FCSTD DOCUMENT  (FreeCAD 1.0R39285 (Git))
Label: mintyCube
License: All rights reserved
LicenseURL: https://en.wikipedia.org/wiki/All_rights_reserved
objects: Part::Cylinder×42, Part::Feature×41, Part::MultiFuse×27, Part::Box×18, Part::Cut×18, Part::Fillet×18, Sketcher::SketchObject×11, Part::Extrusion×10, App::Part×5, Part::FeaturePython×3, Part::Scale×3
note: 202 computed .brp shape members not serialized (recipe doc carries the construction recipe); baked Part::Feature solids carry a one-line shape summary decoded from their .brp

FEATURE [Part::Box] Box  label="outer"
  AttacherType = Attacher::AttachEngine3D
  Height = 79
  Length = 90
  Width = 90
FEATURE [Part::Box] Box001  label="inner"
  AttacherType = Attacher::AttachEngine3D
  Height = 74
  Length = 80
  Placement = pos=(5,5,0) rot=(0,0,1;0rad)
  Width = 80
FEATURE [Part::Cut] Cut  label="hollow_cut"
  Base = -> Box
  Refine = true
  Tool = -> Box001
FEATURE [Part::Fillet] Fillet  label="topCover"
  Base = -> Cut
  EdgeLinks = -> Cut [Edge1,Edge2,Edge3,Edge6,Edge7,Edge8,Edge9,Edge11,Edge17,Edge18,Edge19,Edge20,Edge21,Edge22,Edge23,Edge24]
  Edges = 16 edges: [Edge1 r=8,Edge2 r=8,Edge3 r=8,Edge6 r=8,Edge7 r=8,Edge8 r=8,Edge9 r=8,Edge11 r=8,Edge17 r=7,Edge18 r=7,Edge19 r=7,Edge20 r=7,Edge21 r=7,Edge22 r=7,Edge23 r=7,Edge24 r=7]
  Placement = pos=(0,0,6) rot=(0,0,1;0rad)
FEATURE [Part::Feature] Part__Feature010  label="ips7100"
  Placement = pos=(67.5,20.25,11.095) rot=(0,0,1;0rad)
  shape: bbox 48.08 x 13.99 x 44.08 mm, 1935 faces (baked)
FEATURE [Part::Cylinder] Cylinder003
  Angle = 360
  AttacherType = Attacher::AttachEngine3D
  FirstAngle = 0
  Height = 1
  Placement = pos=(0,0,-25) rot=(0,0,1;0rad)
  Radius = 23
  SecondAngle = 0
FEATURE [Part::Feature] Part__Feature3679  label="Sheel001"
  shape: bbox 121.8 x 121.8 x 8.7 mm, 646 faces (baked)
FEATURE [Part::MultiFuse] Fusion024  label="base001"
  Refine = true
  Shapes = -> [Part__Feature3679,Cylinder003]
FEATURE [Part::FeaturePython] Clone  label="base002"  # Draft clone (typed FeaturePython)
  AttacherType = Attacher::AttachEngine3D
  Fuse = false
  Objects = -> [Fusion024]
  Placement = pos=(45,45,11.66) rot=(0,0,1;0rad)
  Scale = (0.629921,0.629921,0.629921)
FEATURE [Sketcher::SketchObject] Sketch
  ArcFitTolerance = 1e-06
  FullyConstrained = true
  MakeInternals = false
  sketch-geometry (11):
    g0: LineSegment StartX=8 StartY=0 StartZ=0 EndX=82 EndY=0 EndZ=0
    g1: LineSegment StartX=90 StartY=8 StartZ=0 EndX=90 EndY=82 EndZ=0
    g2: LineSegment StartX=82 StartY=90 StartZ=0 EndX=8 EndY=90 EndZ=0
    g3: LineSegment StartX=0 StartY=82 StartZ=0 EndX=0 EndY=8 EndZ=0
    g4: ArcOfCircle CenterX=8 CenterY=8 CenterZ=0 NormalX=0 NormalY=0 NormalZ=1 AngleXU=0 Radius=8 StartAngle=3.14159 EndAngle=4.71239
    g5: ArcOfCircle CenterX=82 CenterY=8 CenterZ=0 NormalX=0 NormalY=0 NormalZ=1 AngleXU=0 Radius=8 StartAngle=4.71239 EndAngle=6.28319
    g6: ArcOfCircle CenterX=82 CenterY=82 CenterZ=0 NormalX=0 NormalY=0 NormalZ=1 AngleXU=0 Radius=8 StartAngle=-1.07e-14 EndAngle=1.5708
    g7: ArcOfCircle CenterX=8 CenterY=82 CenterZ=0 NormalX=0 NormalY=0 NormalZ=1 AngleXU=0 Radius=8 StartAngle=1.5708 EndAngle=3.14159
    g8: GeomPoint [constr] X=0 Y=0 Z=0
    g9: GeomPoint [constr] X=90 Y=90 Z=0
    g10: Circle CenterX=45 CenterY=45 CenterZ=0 NormalX=0 NormalY=0 NormalZ=1 AngleXU=0 Radius=36
  constraints (26):
    c: Tangent(g0,g4) = -1.5708
    c: Tangent(g0,g5) = -1.5708
    c: Tangent(g1,g5) = -1.5708
    c: Tangent(g1,g6) = -1.5708
    c: Tangent(g2,g6) = -1.5708
    c: Tangent(g2,g7) = -1.5708
    c: Tangent(g3,g7) = -1.5708
    c: Tangent(g3,g4) = -1.5708
    c: Horizontal(g0)
    c: Horizontal(g2)
    c: Vertical(g1)
    c: Vertical(g3)
    c: Equal(g4,g5)
    c: Equal(g5,g6)
    c: Equal(g6,g7)
    c: PointOnObject(g8,g0)
    c: PointOnObject(g8,g3)
    c: PointOnObject(g9,g1)
    c: PointOnObject(g9,g2)
    c: Radius(g5) = 8
    c: Coincident(g8,g-1)
    c: Distance(g-1,g2) = 90
    c: Distance(g-2,g1) = 90
    c: DistanceY(g-1,g10) = 45
    c: DistanceX(g-1,g10) = 45
    c: Diameter(g10) = 72
FEATURE [Part::Extrusion] Extrude  label="basePlate"
  Base = -> Sketch
  Dir = (0,0,1)
  DirMode = 2
  FaceMakerClass = Part::FaceMakerBullseye
  FaceMakerMode = 3
  LengthFwd = 11
  LengthRev = 0
  Solid = true
  Symmetric = false
FEATURE [Part::Fillet] Fillet001
  Base = -> Extrude
  EdgeLinks = -> Extrude [Edge26]
  Edges = 1 edges r=1: [Edge26]
FEATURE [Part::MultiFuse] Fusion  label="joinedBase"
  Placement = pos=(0,0,-5) rot=(0,0,1;0rad)
  Refine = true
  Shapes = -> [Clone,Fillet001]
FEATURE [Part::Fillet] Fillet002  label="Bottom"
  Base = -> Fusion
  EdgeLinks = -> Fusion [Edge1318,Edge1319,Edge1320,Edge1321,Edge1322,Edge1323,Edge1324,Edge1325]
  Edges = 8 edges r=7: [Edge1318,Edge1319,Edge1320,Edge1321,Edge1322,Edge1323,Edge1324,Edge1325]
FEATURE [Sketcher::SketchObject] Sketch001
  ArcFitTolerance = 1e-06
  FullyConstrained = true
  MakeInternals = false
  sketch-geometry (16):
    g0: LineSegment StartX=24 StartY=34 StartZ=0 EndX=24 EndY=24 EndZ=0
    g1: LineSegment StartX=24 StartY=24 StartZ=0 EndX=34 EndY=24 EndZ=0
    g2: LineSegment StartX=34 StartY=24 StartZ=0 EndX=34 EndY=34 EndZ=0
    g3: LineSegment StartX=34 StartY=34 StartZ=0 EndX=24 EndY=34 EndZ=0
    g4: LineSegment StartX=66 StartY=34 StartZ=0 EndX=66 EndY=24 EndZ=0
    g5: LineSegment StartX=66 StartY=24 StartZ=0 EndX=56 EndY=24 EndZ=0
    g6: LineSegment StartX=56 StartY=24 StartZ=0 EndX=56 EndY=34 EndZ=0
    g7: LineSegment StartX=56 StartY=34 StartZ=0 EndX=66 EndY=34 EndZ=0
    g8: LineSegment StartX=24 StartY=66 StartZ=0 EndX=24 EndY=56 EndZ=0
    g9: LineSegment StartX=24 StartY=56 StartZ=0 EndX=34 EndY=56 EndZ=0
    g10: LineSegment StartX=34 StartY=56 StartZ=0 EndX=34 EndY=66 EndZ=0
    g11: LineSegment StartX=34 StartY=66 StartZ=0 EndX=24 EndY=66 EndZ=0
    g12: LineSegment StartX=56 StartY=66 StartZ=0 EndX=56 EndY=56 EndZ=0
    g13: LineSegment StartX=56 StartY=56 StartZ=0 EndX=66 EndY=56 EndZ=0
    g14: LineSegment StartX=66 StartY=56 StartZ=0 EndX=66 EndY=66 EndZ=0
    g15: LineSegment StartX=66 StartY=66 StartZ=0 EndX=56 EndY=66 EndZ=0
  constraints (48):
    c: Coincident(g0,g1)
    c: Coincident(g1,g2)
    c: Coincident(g2,g3)
    c: Coincident(g3,g0)
    c: Vertical(g0)
    c: Vertical(g2)
    c: Horizontal(g1)
    c: Horizontal(g3)
    c: Coincident(g4,g5)
    c: Coincident(g5,g6)
    c: Coincident(g6,g7)
    c: Coincident(g7,g4)
    c: Vertical(g4)
    c: Vertical(g6)
    c: Horizontal(g5)
    c: Horizontal(g7)
    c: DistanceX(g1,g1) = 10
    c: Distance(g-1,g1) = 24
    c: DistanceX(g-1,g0) = 24
    c: DistanceY(g0,g0) = 10
    c: Distance(g4,g-1) = 24
    c: Distance(g4,g-2) = 66
    c: Distance(g5,g5) = 10
    c: DistanceY(g4,g4) = 10
    c: Coincident(g8,g9)
    c: Coincident(g9,g10)
    c: Coincident(g10,g11)
    c: Coincident(g11,g8)
    c: Vertical(g8)
    c: Vertical(g10)
    c: Horizontal(g9)
    c: Horizontal(g11)
    c: Coincident(g12,g13)
    c: Coincident(g13,g14)
    c: Coincident(g14,g15)
    c: Coincident(g15,g12)
    c: Vertical(g12)
    c: Vertical(g14)
    c: Horizontal(g13)
    c: Horizontal(g15)
    c: DistanceY(g8,g8) = 10
    c: DistanceX(g9,g9) = 10
    c: Distance(g8,g-2) = 24
    c: Distance(g8,g-1) = 56
    c: DistanceY(g14,g14) = 10
    c: DistanceX(g15,g15) = 10
    c: Distance(g-1,g13) = 56
    c: Distance(g14,g-2) = 66
FEATURE [Part::Feature] Part__Feature334  label="CAPC-0805-T0.95-BN v012"
  Placement = pos=(-5.48627,2.66154,1.6) rot=(0,0,-1;1.5708rad)
  shape: bbox 1.35 x 2.1 x 0.95 mm, 42 faces (baked)
FEATURE [Part::Feature] Part__Feature335  label="CAPC-0805-T0.95-BN v013"
  Placement = pos=(-3.43627,2.66154,1.6) rot=(0,0,-1;1.5708rad)
  shape: bbox 1.35 x 2.1 x 0.95 mm, 42 faces (baked)
FEATURE [Part::Feature] Part__Feature336  label="CAPC-0603-T0.9-BN v009"
  Placement = pos=(-1.69987,-3.28475,1.6) rot=(0,0,1;0rad)
  shape: bbox 1.7 x 0.9 x 0.9 mm, 42 faces (baked)
FEATURE [Part::Feature] Part__Feature337  label="BODY_MF06A003"
  Placement = pos=(0,0,0.762) rot=(0.57735,-0.57735,-0.57735;2.0944rad)
  shape: bbox 1.601 x 2.921 x 1.016 mm, 42 faces (baked)
FEATURE [Part::Feature] Part__Feature338  label="LEAD_MF06A018"
  Placement = pos=(-0.9652,-0.9525,0.1016) rot=(0.57735,-0.57735,-0.57735;2.0944rad)
  shape: bbox 0.6223 x 0.3749 x 0.8636 mm, 14 faces (baked)
FEATURE [Part::Feature] Part__Feature339  label="LEAD_MF06A019"
  Placement = pos=(-0.9652,0,0.1016) rot=(0.57735,-0.57735,-0.57735;2.0944rad)
  shape: bbox 0.6223 x 0.3749 x 0.8636 mm, 14 faces (baked)
FEATURE [Part::Feature] Part__Feature340  label="LEAD_MF06A020"
  Placement = pos=(-0.9652,0.9525,0.1016) rot=(0.57735,-0.57735,-0.57735;2.0944rad)
  shape: bbox 0.6223 x 0.3749 x 0.8636 mm, 14 faces (baked)
FEATURE [Part::Feature] Part__Feature341  label="LEAD_MF06A021"
  Placement = pos=(0.9652,-0.9525,0.1016) rot=(0.57735,0.57735,0.57735;2.0944rad)
  shape: bbox 0.6223 x 0.3749 x 0.8636 mm, 14 faces (baked)
FEATURE [Part::Feature] Part__Feature342  label="LEAD_MF06A022"
  Placement = pos=(0.9652,0,0.1016) rot=(0.57735,0.57735,0.57735;2.0944rad)
  shape: bbox 0.6223 x 0.3749 x 0.8636 mm, 14 faces (baked)
FEATURE [Part::Feature] Part__Feature343  label="LEAD_MF06A023"
  Placement = pos=(0.9652,0.9525,0.1016) rot=(0.57735,0.57735,0.57735;2.0944rad)
  shape: bbox 0.6223 x 0.3749 x 0.8636 mm, 14 faces (baked)
FEATURE [Part::Feature] Part__Feature344  label="SOT363 v005"
  Placement = pos=(4.97054,-0.645171,1.675) rot=(0,0,1;3.14159rad)
  shape: bbox 2.1 x 2 x 1.1 mm, 94 faces, 7 solids (baked)
FEATURE [Part::Feature] Part__Feature345  label="LED 0603 single color v005"
  Placement = pos=(-9.18406,3.72778,1.60762) rot=(0,0,1;1.5708rad)
  shape: bbox 1.961 x 0.7932 x 0.7145 mm, 63 faces, 5 solids (baked)
FEATURE [Part::Feature] Part__Feature346  label="RESC-0603 v007"
  Placement = pos=(4.83432,-3.67461,1.6) rot=(0,0,1;0rad)
  shape: bbox 1.7 x 0.9 x 0.55 mm, 52 faces, 3 solids (baked)
FEATURE [Part::Feature] Part__Feature347  label="RESC-0603 v008"
  Placement = pos=(-7.14949,3.61248,1.6) rot=(0,0,-1;1.5708rad)
  shape: bbox 0.9 x 1.7 x 0.55 mm, 52 faces, 3 solids (baked)
FEATURE [Part::Feature] Part__Feature348  label="Printed Circuit Board004"
  shape: bbox 25.4 x 17.78 x 1.6 mm, 42 faces (baked)
FEATURE [Part::Feature] Part__Feature349  label="EAHC2835WD009"
  shape: bbox 3.513 x 2.813 x 0.7485 mm, 108 faces, 4 solids (baked)
FEATURE [Part::Feature] Part__Feature350  label="AS7341 v005"
  Placement = pos=(0,-0.339822,1.6) rot=(0,0,1;0rad)
  shape: bbox 2 x 3.1 x 1.1 mm, 267 faces, 26 solids (baked)
FEATURE [Part::Feature] Part__Feature351  label="CAPC-0805-T0.95-BN v014"
  Placement = pos=(-5.01759,-3.15294,1.6) rot=(0,0,1;0rad)
  shape: bbox 2.1 x 1.35 x 0.95 mm, 42 faces (baked)
FEATURE [Part::Feature] Part__Feature352  label="YC164_RESPACK v007"
  Placement = pos=(2.99591,1.52916,1.6) rot=(0,0,1;0rad)
  shape: bbox 3.2 x 1.6 x 0.61 mm, 172 faces (baked)
FEATURE [Part::Feature] Part__Feature353  label="qwicc v009"
  Placement = pos=(-10.8364,0.0607456,1.65) rot=(0,0,-1;1.5708rad)
  shape: bbox 4.95 x 6 x 2.96 mm, 229 faces, 7 solids (baked)
FEATURE [Part::Feature] Part__Feature354  label="qwicc v010"
  Placement = pos=(10.8256,0.00556102,1.65) rot=(0,0,1;1.5708rad)
  shape: bbox 4.95 x 6 x 2.96 mm, 229 faces, 7 solids (baked)
FEATURE [App::Part] sot_23_6_v005  label="sot-23-6 v005"
  Group = -> [Part__Feature337,Part__Feature338,Part__Feature339,Part__Feature340,Part__Feature341,Part__Feature342,Part__Feature343]
  Origin = -> Origin091
  Placement = pos=(-4.47945,-0.603742,1.69152) rot=(0,0,1;0rad)
FEATURE [App::Part] Adafruit_AS7341_STEMMA_QT_v005  label="bme280"
  Group = -> [Part__Feature348,Part__Feature349,Part__Feature350,Part__Feature351,Part__Feature334,Part__Feature335,Part__Feature336,sot_23_6_v005,Part__Feature344,Part__Feature345,Part__Feature346,Part__Feature347,Part__Feature352,Part__Feature353,Part__Feature354]
  Origin = -> Origin092
  Placement = pos=(73,47.4039,34) rot=(-0.576812,0.578425,0.576812;4.1904rad)
FEATURE [Part::Box] Box002  label="Cube"
  AttacherType = Attacher::AttachEngine3D
  Height = 6
  Length = 19.2
  Width = 16.5
FEATURE [Part::Cylinder] Cylinder
  Angle = 360
  AttacherType = Attacher::AttachEngine3D
  FirstAngle = 0
  Height = 6
  Placement = pos=(9.6,21.3,0) rot=(0,0,1;0rad)
  Radius = 9.75
  SecondAngle = 0
FEATURE [Part::Box] Box003  label="Cube001"
  AttacherType = Attacher::AttachEngine3D
  Height = 6
  Length = 4.5
  Placement = pos=(13.42,28.5,0) rot=(0,0,1;5.49779rad)
  Width = 5
FEATURE [Part::Fillet] Fillet004
  Base = -> Box003
  EdgeLinks = -> Box003 [Edge3,Edge7]
  Edges = 2 edges r=2.24: [Edge3,Edge7]
FEATURE [Part::Fillet] Fillet005
  Base = -> Box002
  EdgeLinks = -> Box002 [Edge1,Edge3,Edge5,Edge7]
  Edges = 4 edges r=2: [Edge1,Edge3,Edge5,Edge7]
FEATURE [Part::Box] Box005  label="pcb"
  AttacherType = Attacher::AttachEngine3D
  Height = 0.8
  Length = 19.6
  Placement = pos=(-0.2,0,-0.8) rot=(0,0,1;0rad)
  Width = 31.1
FEATURE [Part::Box] Box006  label="Cube004"
  AttacherType = Attacher::AttachEngine3D
  Height = 6
  Length = 4.5
  Placement = pos=(2.6,25.3,0) rot=(0,0,-1;5.49779rad)
  Width = 5
FEATURE [Part::Fillet] Fillet006
  Base = -> Box006
  EdgeLinks = -> Box006 [Edge3,Edge7]
  Edges = 2 edges r=2.24: [Edge3,Edge7]
FEATURE [Part::MultiFuse] Fusion025
  Refine = true
  Shapes = -> [Cylinder,Fillet004,Fillet005,Fillet006]
FEATURE [Part::Fillet] Fillet007  label="COZIR-LP-5000"
  Base = -> Fusion025
  EdgeLinks = -> Fusion025 [Edge2,Edge4,Edge20,Edge26,Edge28,Edge44]
  Edges = 6 edges: [Edge2 r=2,Edge4 r=2,Edge20 r=2,Edge26 r=1,Edge28 r=2,Edge44 r=1]
FEATURE [Part::Feature] Part__Feature3681  label="Document"
  shape: bbox 7.62 x 3.4 x 1.5 mm, 124 faces (baked)
FEATURE [Part::Feature] Part__Feature3682  label="Document001"
  shape: bbox 0.4 x 0.4 x 7.6 mm, 14 faces (baked)
FEATURE [Part::Feature] Part__Feature3683  label="Document002"
  shape: bbox 0.4 x 0.4 x 7.6 mm, 14 faces (baked)
FEATURE [Part::Feature] Part__Feature3684  label="Document003"
  shape: bbox 0.4 x 0.4 x 7.6 mm, 14 faces (baked)
FEATURE [Part::Feature] Part__Feature3685  label="Document004"
  shape: bbox 0.4 x 0.4 x 7.6 mm, 14 faces (baked)
FEATURE [Part::Feature] Part__Feature3686  label="Document005"
  shape: bbox 0.4 x 0.4 x 7.6 mm, 14 faces (baked)
FEATURE [Part::Feature] Part__Feature3687  label="Document006"
  shape: bbox 0.4 x 0.4 x 7.6 mm, 14 faces (baked)
FEATURE [Part::Feature] Part__Feature3688  label="Document007"
  shape: bbox 0.4 x 0.4 x 7.6 mm, 14 faces (baked)
FEATURE [Part::Feature] Part__Feature3689  label="Document008"
  shape: bbox 0.4 x 0.4 x 7.6 mm, 14 faces (baked)
FEATURE [Part::Feature] Part__Feature3690  label="Document009"
  shape: bbox 0.4 x 0.4 x 7.6 mm, 14 faces (baked)
FEATURE [Part::Feature] Part__Feature3691  label="Document010"
  shape: bbox 0.4 x 0.4 x 7.6 mm, 14 faces (baked)
FEATURE [Part::Feature] Part__Feature3692  label="Document011"
  shape: bbox 0.4 x 0.4 x 7.6 mm, 14 faces (baked)
FEATURE [Part::Feature] Part__Feature3693  label="Document012"
  shape: bbox 0.4 x 0.4 x 7.6 mm, 14 faces (baked)
FEATURE [App::Part] Document  label="Document013"
  Group = -> [Part__Feature3681,Part__Feature3682,Part__Feature3683,Part__Feature3684,Part__Feature3685,Part__Feature3686,Part__Feature3687,Part__Feature3688,Part__Feature3689,Part__Feature3690,Part__Feature3691,Part__Feature3692,Part__Feature3693]
  Origin = -> Origin093
  Placement = pos=(9.8,26.75,-0.7) rot=(0,-1,0;3.14159rad)
FEATURE [Part::Cylinder] Cylinder004
  Angle = 360
  AttacherType = Attacher::AttachEngine3D
  FirstAngle = 0
  Height = 1
  Placement = pos=(0,0,-25) rot=(0,0,1;0rad)
  Radius = 23
  SecondAngle = 0
FEATURE [Part::Feature] Part__Feature3694  label="Sheel002"
  shape: bbox 121.8 x 121.8 x 8.7 mm, 646 faces (baked)
FEATURE [Part::MultiFuse] Fusion026  label="base004"
  Refine = true
  Shapes = -> [Part__Feature3694,Cylinder004]
FEATURE [Part::FeaturePython] Clone001  label="base003"  # Draft clone (typed FeaturePython)
  AttacherType = Attacher::AttachEngine3D
  Fuse = false
  Objects = -> [Fusion026]
  Placement = pos=(45,45,6.66) rot=(0,0,1;0rad)
  Scale = (0.629921,0.629921,0.629921)
FEATURE [Part::Scale] Scale
  Base = -> Clone001
  Placement = pos=(45.45,45.45,6.99) rot=(0,0,1;0rad)
  Uniform = true
  UniformScale = 0.99
  XScale = 1
  YScale = 1
  ZScale = 1
FEATURE [Part::Cylinder] Cylinder005
  Angle = 360
  AttacherType = Attacher::AttachEngine3D
  FirstAngle = 0
  Height = 1
  Placement = pos=(0,0,-25) rot=(0,0,1;0rad)
  Radius = 23
  SecondAngle = 0
FEATURE [Part::Feature] Part__Feature3695  label="Sheel003"
  shape: bbox 121.8 x 121.8 x 8.7 mm, 646 faces (baked)
FEATURE [Part::MultiFuse] Fusion027  label="base006"
  Refine = true
  Shapes = -> [Part__Feature3695,Cylinder005]
FEATURE [Part::FeaturePython] Clone002  label="base005"  # Draft clone (typed FeaturePython)
  AttacherType = Attacher::AttachEngine3D
  Fuse = false
  Objects = -> [Fusion027]
  Placement = pos=(45,45,11.66) rot=(0,0,1;0rad)
  Scale = (0.629921,0.629921,0.629921)
FEATURE [Part::Scale] Scale001
  Base = -> Clone002
  Placement = pos=(45.9,45.9,7.5) rot=(0,0,1;0rad)
  Uniform = true
  UniformScale = 0.98
  XScale = 1
  YScale = 1
  ZScale = 1
FEATURE [Sketcher::SketchObject] Sketch002
  ArcFitTolerance = 1e-06
  FullyConstrained = true
  MakeInternals = false
  sketch-geometry (4):
    g0: ArcOfCircle CenterX=0 CenterY=1.25 CenterZ=0 NormalX=0 NormalY=0 NormalZ=1 AngleXU=0 Radius=2 StartAngle=1e-16 EndAngle=3.14159
    g1: ArcOfCircle CenterX=0 CenterY=-1.25 CenterZ=0 NormalX=0 NormalY=0 NormalZ=1 AngleXU=0 Radius=2 StartAngle=3.14159 EndAngle=6.28319
    g2: LineSegment StartX=2 StartY=1.25 StartZ=0 EndX=2 EndY=-1.25 EndZ=0
    g3: LineSegment StartX=-2 StartY=1.25 StartZ=0 EndX=-2 EndY=-1.25 EndZ=0
  constraints (9):
    c: Tangent(g0,g2) = 1.5708
    c: Tangent(g0,g3) = -1.5708
    c: Tangent(g1,g2) = 1.5708
    c: Tangent(g1,g3) = -1.5708
    c: Equal(g0,g1)
    c: Distance(g0,g1) = 2.5
    c: Symmetric(g0,g1,g-1)
    c: Distance(g-2,g3) = 2
    c: Distance(g-1,g2) = 2
FEATURE [Part::Extrusion] Extrude001
  Base = -> Sketch002
  Dir = (0,0,1)
  DirMode = 2
  FaceMakerClass = Part::FaceMakerBullseye
  FaceMakerMode = 3
  LengthFwd = 2.5
  LengthRev = 0
  Placement = pos=(21.9086,21.9086,-7.10396) rot=(-0.627483,0.259912,-0.733969;1.02758rad)
  Solid = true
  Symmetric = false
FEATURE [Part::Extrusion] Extrude002
  Base = -> Sketch001
  Dir = (0,0,1)
  DirMode = 2
  FaceMakerClass = Part::FaceMakerBullseye
  FaceMakerMode = 3
  LengthFwd = 7
  LengthRev = 0
  Placement = pos=(0,0,-7.2) rot=(0,0,1;0rad)
  Solid = true
  Symmetric = false
FEATURE [Part::Fillet] Fillet008
  Base = -> Extrude002
  EdgeLinks = -> Extrude002 [Edge13,Edge14,Edge17,Edge20,Edge25,Edge26,Edge29,Edge32,Edge37,Edge38,Edge41,Edge44,Edge1,Edge2,Edge5,Edge8]
  Edges = 16 edges r=2: [Edge13,Edge14,Edge17,Edge20,Edge25,Edge26,Edge29,Edge32,Edge37,Edge38,Edge41,Edge44,Edge1,Edge2,Edge5,Edge8]
FEATURE [Part::MultiFuse] Fusion028  label="base_w_FanMount"
  Refine = true
  Shapes = -> [Scale001,Fillet008]
FEATURE [Part::Feature] Part__Feature3696  label="MF40100V1-1000U-A99"
  Placement = pos=(45,45,11) rot=(0,0,1;1.5708rad)
  shape: bbox 40.67 x 41.26 x 10.95 mm, 507 faces (baked)
FEATURE [Part::Cylinder] Cylinder007
  Angle = 180
  AttacherType = Attacher::AttachEngine3D
  FirstAngle = 0
  Height = 66
  Placement = pos=(12,5,66) rot=(-0.57735,-0.57735,-0.57735;4.18879rad)
  Radius = 3
  SecondAngle = 0
FEATURE [Part::Cylinder] Cylinder006
  Angle = 240
  AttacherType = Attacher::AttachEngine3D
  FirstAngle = 0
  Height = 66
  Placement = pos=(12,1.84e-14,66) rot=(0.694747,-0.186157,0.694747;3.50969rad)
  Radius = 5
  SecondAngle = 0
FEATURE [Part::Cylinder] Cylinder008
  Angle = 210
  AttacherType = Attacher::AttachEngine3D
  FirstAngle = 0
  Height = 66
  Placement = pos=(12,1.43e-14,61) rot=(0.694747,0.186157,0.694747;2.77349rad)
  Radius = 5
  SecondAngle = 0
FEATURE [Part::MultiFuse] Fusion029
  Refine = true
  Shapes = -> [Cylinder006,Cylinder007,Cylinder008]
FEATURE [Part::Fillet] Fillet010  label="ventcutLeft"
  Base = -> Fusion029
  EdgeLinks = -> Fusion029 [Edge1,Edge3,Edge11,Edge16]
  Edges = 4 edges: [Edge1 r=1,Edge3 r=1,Edge11 r=1,Edge16 r=0.5]
  Placement = pos=(2e-14,90,0) rot=(0,0,1;4.71239rad)
FEATURE [Part::Cylinder] Cylinder009
  Angle = 240
  AttacherType = Attacher::AttachEngine3D
  FirstAngle = 0
  Height = 66
  Placement = pos=(12,1.84e-14,66) rot=(0.694747,-0.186157,0.694747;3.50969rad)
  Radius = 5
  SecondAngle = 0
FEATURE [Part::Cylinder] Cylinder010
  Angle = 180
  AttacherType = Attacher::AttachEngine3D
  FirstAngle = 0
  Height = 66
  Placement = pos=(12,5,66) rot=(-0.57735,-0.57735,-0.57735;4.18879rad)
  Radius = 3
  SecondAngle = 0
FEATURE [Part::Cylinder] Cylinder011
  Angle = 210
  AttacherType = Attacher::AttachEngine3D
  FirstAngle = 0
  Height = 66
  Placement = pos=(12,1.43e-14,61) rot=(0.694747,0.186157,0.694747;2.77349rad)
  Radius = 5
  SecondAngle = 0
FEATURE [Part::MultiFuse] Fusion030
  Refine = true
  Shapes = -> [Cylinder009,Cylinder010,Cylinder011]
FEATURE [Part::Fillet] Fillet011  label="ventcutRight"
  Base = -> Fusion030
  EdgeLinks = -> Fusion030 [Edge1,Edge3,Edge11,Edge16]
  Edges = 4 edges: [Edge1 r=1,Edge3 r=1,Edge11 r=1,Edge16 r=0.5]
  Placement = pos=(90,-2e-14,0) rot=(0,0,1;1.5708rad)
FEATURE [Part::MultiFuse] Fusion031  label="ventcut"
  Refine = true
  Shapes = -> [Fillet010,Fillet011]
FEATURE [Part::Cut] Cut001  label="topCoverVented"
  Base = -> Fillet
  Refine = true
  Tool = -> Fusion031
FEATURE [Part::Box] Box007  label="Inner"
  AttacherType = Attacher::AttachEngine3D
  Height = 16
  Length = 20
  Placement = pos=(-0.4,-0.5,-2.5) rot=(0,0,1;0rad)
  Width = 44
FEATURE [Part::Box] Box008  label="Outer"
  AttacherType = Attacher::AttachEngine3D
  Height = 15
  Length = 28
  Placement = pos=(-4.4,-3.5,-6) rot=(0,0,1;0rad)
  Width = 35
FEATURE [Part::Cut] Cut002  label="slotCut"
  Base = -> Box008
  Refine = true
  Tool = -> Box007
FEATURE [Part::Box] Box009  label="Cube007"
  AttacherType = Attacher::AttachEngine3D
  Height = 2.75
  Length = 20
  Placement = pos=(-0.4,-0.5,6.25) rot=(0,0,1;0rad)
  Width = 32
FEATURE [Part::Cylinder] Cylinder012
  Angle = 360
  AttacherType = Attacher::AttachEngine3D
  FirstAngle = 0
  Height = 2
  Placement = pos=(9.6,21.3,4.1) rot=(0,0,1;0rad)
  Radius = 9
  SecondAngle = 0
FEATURE [App::Part] Part  label="Cozir"
  Group = -> [Document,Box002,Cylinder,Box003,Fillet004,Fillet005,Box006,Fillet006,Fusion025,Fillet007,Box005,Cylinder012]
  Origin = -> Origin094
  Placement = pos=(5.5,47,35) rot=(0,0,1;4.71239rad)
FEATURE [Part::Box] Box010  label="Cube008"
  AttacherType = Attacher::AttachEngine3D
  Height = 10
  Length = 10
  Placement = pos=(4.8,24,-6) rot=(0,0,1;0rad)
  Width = 20
FEATURE [Part::Cylinder] Cylinder013
  Angle = 360
  AttacherType = Attacher::AttachEngine3D
  FirstAngle = 0
  Height = 5
  Placement = pos=(9.6,21.3,4.1) rot=(0,0,1;0rad)
  Radius = 10
  SecondAngle = 0
FEATURE [Part::MultiFuse] Fusion032  label="sltCover"
  Refine = true
  Shapes = -> [Cut002,Box009]
FEATURE [Part::Cut] Cut003
  Base = -> Fusion032
  Refine = true
  Tool = -> Cylinder013
FEATURE [Part::Cut] Cut004  label="CozirHold"
  Base = -> Cut003
  Placement = pos=(5.5,47,35) rot=(0,0,1;4.71239rad)
  Refine = true
  Tool = -> Box010
FEATURE [Part::MultiFuse] Fusion033  label="topCover_CozirHold"
  Refine = true
  Shapes = -> [Cut001,Cut004]
FEATURE [Part::Box] Box027  label="bottom046"
  AttacherType = Attacher::AttachEngine3D
  Height = 39
  Length = 70
  Placement = pos=(2,2,2) rot=(0,0,1;0rad)
  Width = 87
FEATURE [Part::Box] Box031  label="bottom049"
  AttacherType = Attacher::AttachEngine3D
  Height = 27
  Length = 74
  Width = 91
FEATURE [Part::Fillet] Fillet046  label="bottom047"
  Base = -> Box031
  EdgeLinks = -> Box031 [Edge1,Edge3,Edge4,Edge5,Edge7,Edge8,Edge9,Edge11]
  Edges = 8 edges r=2: [Edge1,Edge3,Edge4,Edge5,Edge7,Edge8,Edge9,Edge11]
FEATURE [Part::Fillet] Fillet050  label="bottomCut013"
  Base = -> Box027
  EdgeLinks = -> Box027 [Edge1,Edge3,Edge4,Edge5,Edge7,Edge8,Edge9,Edge11]
  Edges = 8 edges r=2: [Edge1,Edge3,Edge4,Edge5,Edge7,Edge8,Edge9,Edge11]
FEATURE [Part::Cut] Cut032  label="bottom052"
  Base = -> Fillet046
  Tool = -> Fillet050
FEATURE [Sketcher::SketchObject] Sketch171
  ArcFitTolerance = 0
  AttachmentSupport = -> [Cut032]
  FullyConstrained = true
  MakeInternals = false
  MapMode = 2
  sketch-geometry (10):
    g0: LineSegment StartX=63 StartY=9.25 StartZ=0 EndX=78 EndY=9.25 EndZ=0
    g1: LineSegment StartX=78 StartY=9.25 StartZ=0 EndX=78 EndY=2 EndZ=0
    g2: LineSegment StartX=78 StartY=2 StartZ=0 EndX=63 EndY=2 EndZ=0
    g3: LineSegment StartX=63 StartY=2 StartZ=0 EndX=63 EndY=9.25 EndZ=0
    g4: LineSegment StartX=-5 StartY=9.25 StartZ=0 EndX=10 EndY=9.25 EndZ=0
    g5: LineSegment StartX=10 StartY=9.25 StartZ=0 EndX=10 EndY=2 EndZ=0
    g6: LineSegment StartX=10 StartY=2 StartZ=0 EndX=-5 EndY=2 EndZ=0
    g7: LineSegment StartX=-5 StartY=2 StartZ=0 EndX=-5 EndY=9.25 EndZ=0
    g8: Circle CenterX=7.47 CenterY=6.47 CenterZ=0 NormalX=0 NormalY=0 NormalZ=1 AngleXU=0 Radius=1.35
    g9: Circle CenterX=65.52 CenterY=6.47 CenterZ=0 NormalX=0 NormalY=0 NormalZ=1 AngleXU=0 Radius=1.35
  constraints (30):
    c: Coincident(g0,g1)
    c: Coincident(g1,g2)
    c: Coincident(g2,g3)
    c: Coincident(g3,g0)
    c: Horizontal(g0)
    c: Horizontal(g2)
    c: Vertical(g1)
    c: Vertical(g3)
    c: Coincident(g4,g5)
    c: Coincident(g5,g6)
    c: Coincident(g6,g7)
    c: Coincident(g7,g4)
    c: Horizontal(g4)
    c: Horizontal(g6)
    c: Vertical(g5)
    c: Vertical(g7)
    c: DistanceX(g6) = -5
    c: DistanceY(g6) = 2
    c: DistanceX(g6,g6) = 15
    c: DistanceY(g7,g7) = 7.25
    c: DistanceX(g-1,g1) = 78
    c: DistanceY(g2,g5) = 0
    c: DistanceY(g0,g4) = 0
    c: DistanceX(g2,g2) = 15
    c: DistanceX(g8) = 7.47
    c: Radius(g8) = 1.35
    c: DistanceX(g9) = 65.52
    c: DistanceY(g8,g9) = 0
    c: Radius(g9) = 1.35
    c: DistanceY(g8) = 6.47
FEATURE [Part::Extrusion] Extrude174  label="RaberryPiHold004"
  Base = -> Sketch171
  Dir = (0,0,1)
  DirMode = 2
  FaceMakerClass = Part::FaceMakerBullseye
  FaceMakerMode = 3
  LengthFwd = 2
  LengthRev = 0
  Placement = pos=(0,0,20.7) rot=(0,0,1;0rad)
  Solid = true
  Symmetric = false
FEATURE [Part::Fillet] Fillet044  label="piHoldBottomInDone004"
  Base = -> Extrude174
  EdgeLinks = -> Extrude174 [Edge16,Edge19,Edge27,Edge2,Edge4,Edge7]
  Edges = 6 edges: [Edge16 r=2,Edge19 r=1,Edge27 r=1,Edge2 r=2,Edge4 r=1,Edge7 r=1]
  Placement = pos=(8.5,87.5,73.5) rot=(-1,0,0;3.14159rad)
FEATURE [Part::Box] Box032  label="batteryPlus"
  AttacherType = Attacher::AttachEngine3D
  Height = 11
  Length = 68
  Placement = pos=(11,71,79) rot=(-1,0,0;3.14159rad)
  Width = 56
FEATURE [Sketcher::SketchObject] Sketch153
  ArcFitTolerance = 0
  FullyConstrained = true
  MakeInternals = false
  Placement = pos=(0,0,0) rot=(1,0,0;1.5708rad)
  sketch-geometry (40):
    g0: LineSegment StartX=40 StartY=24.5 StartZ=0 EndX=40 EndY=22 EndZ=0
    g1: LineSegment StartX=40 StartY=22 StartZ=0 EndX=42.5 EndY=19.5 EndZ=0
    g2: LineSegment StartX=42.5 StartY=19.5 StartZ=0 EndX=48.7 EndY=19.5 EndZ=0
    g3: LineSegment StartX=48.7 StartY=19.5 StartZ=0 EndX=51.2 EndY=22 EndZ=0
    g4: LineSegment StartX=51.2 StartY=22 StartZ=0 EndX=51.2 EndY=24.5 EndZ=0
    g5: LineSegment StartX=51.2 StartY=24.5 StartZ=0 EndX=40 EndY=24.5 EndZ=0
    g6: LineSegment StartX=52.45 StartY=24.5 StartZ=0 EndX=52.45 EndY=22 EndZ=0
    g7: LineSegment StartX=52.45 StartY=22 StartZ=0 EndX=54.95 EndY=19.5 EndZ=0
    g8: LineSegment StartX=54.95 StartY=19.5 StartZ=0 EndX=61.15 EndY=19.5 EndZ=0
    g9: LineSegment StartX=61.15 StartY=19.5 StartZ=0 EndX=63.65 EndY=22 EndZ=0
    g10: LineSegment StartX=63.65 StartY=22 StartZ=0 EndX=63.65 EndY=24.5 EndZ=0
    g11: LineSegment StartX=63.65 StartY=24.5 StartZ=0 EndX=52.45 EndY=24.5 EndZ=0
    g12: ArcOfCircle CenterX=12.3 CenterY=15.45 CenterZ=0 NormalX=0 NormalY=0 NormalZ=1 AngleXU=0 Radius=1 StartAngle=1.5708 EndAngle=3.14159
    g13: LineSegment StartX=11.3 StartY=15.45 StartZ=0 EndX=11.3 EndY=14.2 EndZ=0
    g14: LineSegment StartX=12.3 StartY=16.45 StartZ=0 EndX=16.8 EndY=16.45 EndZ=0
    g15: ArcOfCircle CenterX=16.8 CenterY=15.45 CenterZ=0 NormalX=0 NormalY=0 NormalZ=1 AngleXU=0 Radius=1 StartAngle=3e-16 EndAngle=1.5708
    g16: ArcOfCircle CenterX=16.8 CenterY=14.2 CenterZ=0 NormalX=0 NormalY=0 NormalZ=1 AngleXU=0 Radius=1 StartAngle=4.71239 EndAngle=6.28319
    g17: ArcOfCircle CenterX=12.3 CenterY=14.2 CenterZ=0 NormalX=0 NormalY=0 NormalZ=1 AngleXU=0 Radius=1 StartAngle=3.14159 EndAngle=4.71239
    g18: LineSegment StartX=12.3 StartY=13.2 StartZ=0 EndX=16.8 EndY=13.2 EndZ=0
    g19: LineSegment StartX=17.8 StartY=15.45 StartZ=0 EndX=17.8 EndY=14.2 EndZ=0
    g20: Circle CenterX=18.9 CenterY=16.475 CenterZ=0 NormalX=0 NormalY=0 NormalZ=1 AngleXU=0 Radius=0.5
    g21: Circle CenterX=21.09 CenterY=16.475 CenterZ=0 NormalX=0 NormalY=0 NormalZ=1 AngleXU=0 Radius=0.5
    g22: Circle CenterX=23.28 CenterY=16.475 CenterZ=0 NormalX=0 NormalY=0 NormalZ=1 AngleXU=0 Radius=0.5
    g23: Circle CenterX=25.47 CenterY=16.475 CenterZ=0 NormalX=0 NormalY=0 NormalZ=1 AngleXU=0 Radius=0.5
    g24: LineSegment StartX=44.8 StartY=16.45 StartZ=0 EndX=49.3 EndY=16.45 EndZ=0
    g25: LineSegment StartX=50.3 StartY=15.45 StartZ=0 EndX=50.3 EndY=14.2 EndZ=0
    g26: LineSegment StartX=49.3 StartY=13.2 StartZ=0 EndX=44.8 EndY=13.2 EndZ=0
    g27: LineSegment StartX=43.8 StartY=15.45 StartZ=0 EndX=43.8 EndY=14.2 EndZ=0
    g28: ArcOfCircle CenterX=44.8 CenterY=15.45 CenterZ=0 NormalX=0 NormalY=0 NormalZ=1 AngleXU=0 Radius=1 StartAngle=1.5708 EndAngle=3.14159
    g29: ArcOfCircle CenterX=49.3 CenterY=15.45 CenterZ=0 NormalX=0 NormalY=0 NormalZ=1 AngleXU=0 Radius=1 StartAngle=3e-16 EndAngle=1.5708
    g30: ArcOfCircle CenterX=49.3 CenterY=14.2 CenterZ=0 NormalX=0 NormalY=0 NormalZ=1 AngleXU=0 Radius=1 StartAngle=4.71239 EndAngle=6.28319
    g31: ArcOfCircle CenterX=44.8 CenterY=14.2 CenterZ=0 NormalX=0 NormalY=0 NormalZ=1 AngleXU=0 Radius=1 StartAngle=3.14159 EndAngle=4.71239
    g32: LineSegment StartX=52.25 StartY=15.58 StartZ=0 EndX=52.25 EndY=14.58 EndZ=0
    g33: LineSegment StartX=53.5 StartY=16.83 StartZ=0 EndX=60.5 EndY=16.83 EndZ=0
    g34: LineSegment StartX=53.5 StartY=13.33 StartZ=0 EndX=60.5 EndY=13.33 EndZ=0
    g35: LineSegment StartX=61.75 StartY=15.58 StartZ=0 EndX=61.75 EndY=14.58 EndZ=0
    g36: ArcOfCircle CenterX=53.5 CenterY=15.58 CenterZ=0 NormalX=0 NormalY=0 NormalZ=1 AngleXU=0 Radius=1.25 StartAngle=1.5708 EndAngle=3.14159
    g37: ArcOfCircle CenterX=60.5 CenterY=15.58 CenterZ=0 NormalX=0 NormalY=0 NormalZ=1 AngleXU=0 Radius=1.25 StartAngle=2e-16 EndAngle=1.5708
    g38: ArcOfCircle CenterX=60.5 CenterY=14.58 CenterZ=0 NormalX=0 NormalY=0 NormalZ=1 AngleXU=0 Radius=1.25 StartAngle=4.7124 EndAngle=6.28319
    g39: ArcOfCircle CenterX=53.5 CenterY=14.58 CenterZ=0 NormalX=0 NormalY=0 NormalZ=1 AngleXU=0 Radius=1.25 StartAngle=3.14159 EndAngle=4.71239
  constraints (132):
    c: Coincident(g0,g1)
    c: Coincident(g1,g2)
    c: Horizontal(g2)
    c: Coincident(g2,g3)
    c: Coincident(g3,g4)
    c: Vertical(g4)
    c: Coincident(g4,g5)
    c: Coincident(g5,g0)
    c: Coincident(g6,g7)
    c: Coincident(g7,g8)
    c: Horizontal(g8)
    c: Coincident(g8,g9)
    c: Coincident(g9,g10)
    c: Vertical(g10)
    c: Coincident(g10,g11)
    c: Coincident(g11,g6)
    c: Horizontal(g11)
    c: Horizontal(g5)
    c: Vertical(g0)
    c: Vertical(g6)
    c: DistanceX(g0) = 40
    c: DistanceX(g0,g4) = 11.2
    c: DistanceY(g6,g4) = 0
    c: DistanceY(g0,g0) = 2.5
    c: DistanceY(g3,g0) = 0
    c: DistanceY(g6,g3) = 0
    c: DistanceY(g9,g6) = 0
    c: DistanceY(g1,g0) = 2.5
    c: DistanceX(g0,g1) = 2.5
    c: DistanceX(g2,g3) = 2.5
    c: DistanceX(g4,g6) = 1.25
    c: DistanceY(g7,g2) = 0
    c: DistanceX(g6,g7) = 2.5
    c: DistanceX(g8,g9) = 2.5
    c: DistanceX(g6,g10) = 11.2
    c: DistanceY(g0) = 24.5
    c: Coincident(g13,g12)
    c: Vertical(g13)
    c: Horizontal(g14)
    c: Coincident(g15,g14)
    c: Coincident(g17,g13)
    c: Coincident(g18,g17)
    c: Coincident(g18,g16)
    c: Horizontal(g18)
    c: Coincident(g19,g15)
    c: Coincident(g19,g16)
    c: Vertical(g19)
    c: Coincident(g12,g14)
    c: Radius(g12) = 1
    c: Angle(g12) = 1.5708
    c: Angle(g15) = 1.5708
    c: Angle(g16) = 1.5708
    c: Angle(g17) = 1.5708
    c: DistanceX(g17) = 12.3
    c: DistanceY(g17) = 13.2
    c: DistanceX(g13) = 11.3
    c: DistanceY(g17,g13) = 0
    c: DistanceY(g12,g12) = 0
    c: DistanceX(g15,g14) = 0
    c: Radius(g15) = 1
    c: Radius(g16) = 1
    c: DistanceX(g16,g16) = 0
    c: DistanceX(g12,g14) = 4.5
    c: DistanceX(g20) = 18.9
    c: Radius(g20) = 0.5
    c: DistanceY(g20) = 16.475
    c: DistanceX(g20,g21) = 2.19
    c: DistanceY(g20,g21) = 0
    c: DistanceY(g22,g21) = 0
    c: DistanceY(g23,g22) = 0
    c: DistanceX(g21,g22) = 2.19
    c: Radius(g21) = 0.5
    c: Radius(g22) = 0.5
    c: Radius(g23) = 0.5
    c: DistanceX(g22,g23) = 2.19
    c: DistanceY(g17,g12) = 1.25
    c: Horizontal(g24)
    c: Vertical(g25)
    c: Vertical(g27)
    c: Coincident(g27,g28)
    c: Coincident(g27,g31)
    c: Coincident(g26,g31)
    c: Coincident(g26,g30)
    c: Coincident(g25,g30)
    c: Coincident(g25,g29)
    c: Coincident(g24,g29)
    c: Coincident(g24,g28)
    c: Angle(g28) = 1.5708
    c: Angle(g29) = 1.5708
    c: Angle(g31) = 1.5708
    c: Angle(g30) = 1.5708
    c: DistanceY(g12,g28) = 0
    c: DistanceY(g28,g27) = 0
    c: Radius(g28) = 1
    c: DistanceY(g27,g31) = 0
    c: Radius(g31) = 1
    c: Radius(g30) = 1
    c: Radius(g29) = 1
    c: DistanceY(g27,g17) = 0
    c: DistanceY(g25,g30) = 0
    c: Horizontal(g26)
    c: DistanceX(g29,g24) = 0
    c: DistanceX(g26,g26) = 4.5
    c: Vertical(g32)
    c: Horizontal(g33)
    c: Horizontal(g34)
    c: Vertical(g35)
    c: Coincident(g36,g32)
    c: Coincident(g36,g33)
    c: Coincident(g37,g33)
    c: Coincident(g39,g32)
    c: Coincident(g39,g34)
    c: Coincident(g34,g38)
    c: Coincident(g35,g38)
    c: Coincident(g35,g37)
    c: DistanceX(g36) = 53.5
    c: DistanceY(g36) = 15.58
    c: DistanceX(g36,g39) = 0
    c: DistanceY(g39,g36) = 1
    c: Radius(g36) = 1.25
    c: Radius(g38) = 1.25
    c: Radius(g37) = 1.25
    c: DistanceX(g39,g34) = 0
    c: DistanceX(g36,g33) = 0
    c: DistanceY(g36,g37) = 0
    c: DistanceY(g38,g39) = 0
    c: DistanceY(g39,g32) = 0
    c: DistanceX(g36,g37) = 7
    c: DistanceX(g12,g28) = 32.5
    c: DistanceY(g35,g38) = 0
    c: DistanceY(g37,g35) = 0
    c: Angle(g36) = 1.5708
FEATURE [Part::Extrusion] Extrude153  label="lightBottomCutDone004"
  Base = -> Sketch153
  Dir = (0,-1,2e-16)
  DirMode = 2
  FaceMakerClass = Part::FaceMakerBullseye
  FaceMakerMode = 3
  LengthFwd = 10
  LengthRev = 0
  Placement = pos=(8.25,84,74) rot=(-1,0,0;3.14159rad)
  Solid = true
  Symmetric = false
FEATURE [Part::Cut] Cut033  label="topCover_portCut"
  Base = -> Fusion033
  Refine = true
  Tool = -> Extrude153
FEATURE [Sketcher::SketchObject] Sketch172
  ArcFitTolerance = 1e-06
  FullyConstrained = true
  MakeInternals = false
  Placement = pos=(0,0,0) rot=(0,0.707107,0.707107;3.14159rad)
  sketch-geometry (4):
    g0: ArcOfCircle CenterX=-67 CenterY=55 CenterZ=0 NormalX=0 NormalY=0 NormalZ=1 AngleXU=0 Radius=10 StartAngle=1.5708 EndAngle=4.71239
    g1: ArcOfCircle CenterX=-23 CenterY=55 CenterZ=0 NormalX=0 NormalY=0 NormalZ=1 AngleXU=0 Radius=10 StartAngle=4.71239 EndAngle=7.85398
    g2: LineSegment StartX=-67 StartY=65 StartZ=0 EndX=-23 EndY=65 EndZ=0
    g3: LineSegment StartX=-67 StartY=45 StartZ=0 EndX=-23 EndY=45 EndZ=0
  constraints (10):
    c: Tangent(g0,g2) = 1.5708
    c: Tangent(g0,g3) = -1.5708
    c: Tangent(g1,g2) = 1.5708
    c: Tangent(g1,g3) = -1.5708
    c: Equal(g0,g1)
    c: Horizontal(g2)
    c: DistanceY(g1,g1) = 20
    c: Distance(g0,g-1) = 45
    c: Distance(g1,g-2) = 23
    c: DistanceX(g3,g3) = 44
FEATURE [Part::Extrusion] Extrude175
  Base = -> Sketch172
  Dir = (0,1,-2e-16)
  DirMode = 2
  FaceMakerClass = Part::FaceMakerBullseye
  FaceMakerMode = 3
  LengthFwd = 4
  LengthRev = 0
  Placement = pos=(0,86,0) rot=(0,0,1;0rad)
  Solid = true
  Symmetric = false
FEATURE [Part::Cut] Cut034
  Base = -> Cut033
  Refine = true
  Tool = -> Extrude175
FEATURE [Part::Fillet] Fillet051  label="topCoverFillet"
  Base = -> Cut034
  EdgeLinks = -> Cut034 [Edge67,Edge68,Edge69,Edge70,Edge91,Edge92,Edge93,Edge94,Edge151,Edge153,Edge155,Edge156,Edge183,Edge184,Edge185,Edge187,Edge188,Edge189,Edge190,Edge191,Edge192,Edge193,Edge194,Edge195,Edge288,Edge289,Edge290,Edge292,Edge293,Edge294,Edge298,Edge300,Edge301,Edge303,Edge304,Edge305,Edge306,Edge311,Edge314]
  Edges = 39 edges: [Edge67 r=2,Edge68 r=2,Edge69 r=2,Edge70 r=2,Edge91 r=2,Edge92 r=2,Edge93 r=2,Edge94 r=2,Edge151 r=1.5,Edge153 r=1.5,Edge155 r=1.5,Edge156 r=1.5,Edge183 r=1,Edge184 r=2,Edge185 r=2,Edge187 r=1,Edge188 r=2,Edge189 r=1,Edge190 r=1,Edge191 r=1,Edge192 r=1,Edge193 r=1,Edge194 r=2,Edge195 r=1,Edge288 r=2,Edge289 r=1,Edge290 r=1,Edge292 r=1,Edge293 r=1,Edge294 r=2,Edge298 r=2,Edge300 r=2,Edge301 r=1,Edge303 r=1,Edge304 r=1,Edge305 r=1,Edge306 r=1,Edge311 r=1,Edge314 r=1]
FEATURE [Sketcher::SketchObject] Sketch173
  ArcFitTolerance = 1e-06
  FullyConstrained = true
  MakeInternals = false
  Placement = pos=(0,0,0) rot=(1,0,0;3.14159rad)
  sketch-geometry (4):
    g0: Circle CenterX=12 CenterY=-12 CenterZ=0 NormalX=0 NormalY=0 NormalZ=1 AngleXU=0 Radius=1.625
    g1: Circle CenterX=78 CenterY=-12 CenterZ=0 NormalX=0 NormalY=0 NormalZ=1 AngleXU=0 Radius=1.625
    g2: Circle CenterX=12 CenterY=-78 CenterZ=0 NormalX=0 NormalY=0 NormalZ=1 AngleXU=0 Radius=1.625
    g3: Circle CenterX=78 CenterY=-78 CenterZ=0 NormalX=0 NormalY=0 NormalZ=1 AngleXU=0 Radius=1.625
  constraints (12):
    c: Equal(g0,g1)
    c: Equal(g0,g2)
    c: Equal(g0,g3)
    c: Diameter(g0) = 3.25
    c: Distance(g0,g-1) = 12
    c: Distance(g0,g-2) = 12
    c: Distance(g1,g-2) = 78
    c: Distance(g1,g-1) = 12
    c: Distance(g2,g-2) = 12
    c: Distance(g2,g-1) = 78
    c: DistanceY(g3,g-1) = 78
    c: DistanceX(g-1,g3) = 78
FEATURE [Part::Extrusion] Extrude176
  Base = -> Sketch173
  Dir = (0,0,-1)
  DirMode = 2
  FaceMakerClass = Part::FaceMakerBullseye
  FaceMakerMode = 3
  LengthFwd = 20
  LengthRev = 0
  Solid = true
  Symmetric = true
FEATURE [Sketcher::SketchObject] Sketch167
  ArcFitTolerance = 0
  FullyConstrained = true
  MakeInternals = false
  sketch-geometry (5):
    g0: ArcOfCircle CenterX=6.5 CenterY=41 CenterZ=0 NormalX=0 NormalY=0 NormalZ=1 AngleXU=0 Radius=5 StartAngle=4.71239 EndAngle=7.85398
    g1: LineSegment StartX=6.5 StartY=46 StartZ=0 EndX=2 EndY=46 EndZ=0
    g2: LineSegment StartX=6.5 StartY=36 StartZ=0 EndX=2 EndY=36 EndZ=0
    g3: LineSegment StartX=2 StartY=46 StartZ=0 EndX=2 EndY=36 EndZ=0
    g4: Circle CenterX=6.5 CenterY=41 CenterZ=0 NormalX=0 NormalY=0 NormalZ=1 AngleXU=0 Radius=1.65
  constraints (15):
    c: Coincident(g1,g0)
    c: Coincident(g2,g0)
    c: Horizontal(g2)
    c: Coincident(g3,g1)
    c: Coincident(g3,g2)
    c: Vertical(g3)
    c: Horizontal(g1)
    c: DistanceX(g0,g0) = 0
    c: DistanceX(g2) = 2
    c: DistanceY(g2) = 36
    c: DistanceY(g2,g1) = 10
    c: Angle(g0) = 3.14159
    c: DistanceX(g0) = 6.5
    c: Coincident(g4,g0)
    c: Radius(g4) = 1.65
FEATURE [Part::Extrusion] Extrude163  label="batteryHold01"
  Base = -> Sketch167
  Dir = (0,0,1)
  DirMode = 2
  FaceMakerClass = Part::FaceMakerBullseye
  FaceMakerMode = 3
  LengthFwd = 5
  LengthRev = 0
  Placement = pos=(4,87,66) rot=(0,0,1;4.71239rad)
  Solid = true
  Symmetric = false
FEATURE [Sketcher::SketchObject] Sketch174
  ArcFitTolerance = 0
  FullyConstrained = true
  MakeInternals = false
  sketch-geometry (5):
    g0: ArcOfCircle CenterX=6.5 CenterY=41 CenterZ=0 NormalX=0 NormalY=0 NormalZ=1 AngleXU=0 Radius=5 StartAngle=4.71239 EndAngle=7.85398
    g1: LineSegment StartX=6.5 StartY=46 StartZ=0 EndX=2 EndY=46 EndZ=0
    g2: LineSegment StartX=6.5 StartY=36 StartZ=0 EndX=2 EndY=36 EndZ=0
    g3: LineSegment StartX=2 StartY=46 StartZ=0 EndX=2 EndY=36 EndZ=0
    g4: Circle CenterX=6.5 CenterY=41 CenterZ=0 NormalX=0 NormalY=0 NormalZ=1 AngleXU=0 Radius=1.65
  constraints (15):
    c: Coincident(g1,g0)
    c: Coincident(g2,g0)
    c: Horizontal(g2)
    c: Coincident(g3,g1)
    c: Coincident(g3,g2)
    c: Vertical(g3)
    c: Horizontal(g1)
    c: DistanceX(g0,g0) = 0
    c: DistanceX(g2) = 2
    c: DistanceY(g2) = 36
    c: DistanceY(g2,g1) = 10
    c: Angle(g0) = 3.14159
    c: DistanceX(g0) = 6.5
    c: Coincident(g4,g0)
    c: Radius(g4) = 1.65
FEATURE [Part::Extrusion] Extrude177  label="batteryHold02"
  Base = -> Sketch174
  Dir = (0,0,1)
  DirMode = 2
  FaceMakerClass = Part::FaceMakerBullseye
  FaceMakerMode = 3
  LengthFwd = 5
  LengthRev = 0
  Placement = pos=(86,3,66) rot=(0,0,-1;4.71239rad)
  Solid = true
  Symmetric = false
FEATURE [Sketcher::SketchObject] Sketch175
  ArcFitTolerance = 1e-06
  FullyConstrained = false
  MakeInternals = false
  Placement = pos=(0,0,0) rot=(1,0,0;3.14159rad)
  sketch-geometry (12):
    g0: LineSegment StartX=25 StartY=-15 StartZ=0 EndX=75 EndY=-15 EndZ=0
    g1: LineSegment StartX=75 StartY=-15 StartZ=0 EndX=75 EndY=-71 EndZ=0
    g2: LineSegment StartX=75 StartY=-71 StartZ=0 EndX=25 EndY=-71 EndZ=0
    g3: LineSegment StartX=25 StartY=-71 StartZ=0 EndX=25 EndY=-64 EndZ=0
    g4: LineSegment StartX=25 StartY=-64 StartZ=0 EndX=70 EndY=-64 EndZ=0
    g5: LineSegment StartX=70 StartY=-64 StartZ=0 EndX=41.096 EndY=-43 EndZ=0
    g6: LineSegment StartX=41.096 StartY=-43 StartZ=0 EndX=70 EndY=-22 EndZ=0
    g7: LineSegment StartX=25 StartY=-15 StartZ=0 EndX=25 EndY=-22 EndZ=0
    g8: LineSegment StartX=25 StartY=-22 StartZ=0 EndX=70 EndY=-22 EndZ=0
    g9: LineSegment StartX=70 StartY=-28.5199 StartZ=0 EndX=49.3543 EndY=-43.5199 EndZ=0
    g10: LineSegment StartX=49.3543 StartY=-43.5199 StartZ=0 EndX=70 EndY=-58.5199 EndZ=0
    g11: LineSegment StartX=70 StartY=-58.5199 StartZ=0 EndX=70 EndY=-28.5199 EndZ=0
  constraints (34):
    c: Horizontal(g0)
    c: Coincident(g1,g0)
    c: Vertical(g1)
    c: Coincident(g2,g1)
    c: Horizontal(g2)
    c: Coincident(g3,g2)
    c: Vertical(g3)
    c: Coincident(g4,g3)
    c: Horizontal(g4)
    c: Coincident(g5,g4)
    c: Coincident(g6,g5)
    c: Coincident(g7,g0)
    c: Vertical(g7)
    c: Coincident(g8,g7)
    c: Coincident(g8,g6)
    c: Horizontal(g8)
    c: Coincident(g10,g9)
    c: Coincident(g11,g10)
    c: Coincident(g11,g9)
    c: Distance(g0,g-1) = 15
    c: Vertical(g11)
    c: DistanceX(g0,g0) = 50
    c: Distance(g1,g11) = 5
    c: DistanceY(g7,g7) = 7
    c: Equal(g6,g5)
    c: Distance(g0,g-2) = 25
    c: DistanceX(g8,g8) = 45
    c: DistanceX(g4,g4) = 45
    c: Distance(g3,g-2) = 25
    c: DistanceY(g3,g3) = 7
    c: DistanceY(g3,g7) = 42
    c: Equal(g9,g10)
    c: Angle(g8,g6) = 0.628319
    c: Angle(g8,g9) = 0.628319
FEATURE [Part::Cylinder] Cylinder014
  Angle = 240
  AttacherType = Attacher::AttachEngine3D
  FirstAngle = 0
  Height = 44
  Placement = pos=(12,1.84e-14,66) rot=(0.694747,-0.186157,0.694747;3.50969rad)
  Radius = 5
  SecondAngle = 0
FEATURE [Part::Cylinder] Cylinder015
  Angle = 180
  AttacherType = Attacher::AttachEngine3D
  FirstAngle = 0
  Height = 44
  Placement = pos=(12,5,66) rot=(-0.57735,-0.57735,-0.57735;4.18879rad)
  Radius = 3
  SecondAngle = 0
FEATURE [Part::Cylinder] Cylinder016
  Angle = 210
  AttacherType = Attacher::AttachEngine3D
  FirstAngle = 0
  Height = 44
  Placement = pos=(12,1.43e-14,61) rot=(0.694747,0.186157,0.694747;2.77349rad)
  Radius = 5
  SecondAngle = 0
FEATURE [Part::Cylinder] Cylinder017
  Angle = 240
  AttacherType = Attacher::AttachEngine3D
  FirstAngle = 0
  Height = 44
  Placement = pos=(12,1.84e-14,66) rot=(0.694747,-0.186157,0.694747;3.50969rad)
  Radius = 5
  SecondAngle = 0
FEATURE [Part::Cylinder] Cylinder018
  Angle = 180
  AttacherType = Attacher::AttachEngine3D
  FirstAngle = 0
  Height = 44
  Placement = pos=(12,5,66) rot=(-0.57735,-0.57735,-0.57735;4.18879rad)
  Radius = 3
  SecondAngle = 0
FEATURE [Part::Cylinder] Cylinder019
  Angle = 210
  AttacherType = Attacher::AttachEngine3D
  FirstAngle = 0
  Height = 44
  Placement = pos=(12,1.43e-14,61) rot=(0.694747,0.186157,0.694747;2.77349rad)
  Radius = 5
  SecondAngle = 0
FEATURE [Part::MultiFuse] Fusion034
  Refine = true
  Shapes = -> [Cylinder014,Cylinder015,Cylinder016]
FEATURE [Part::Fillet] Fillet052  label="ventcutLeft001"
  Base = -> Fusion034
  EdgeLinks = -> Fusion034 [Edge1,Edge3,Edge16]
  Edges = 3 edges: [Edge1 r=1,Edge3 r=1,Edge16 r=0.5]
  Placement = pos=(140,3.41e-14,7.5) rot=(0,1,0;4.71239rad)
FEATURE [Part::MultiFuse] Fusion035
  Refine = true
  Shapes = -> [Cylinder017,Cylinder018,Cylinder019]
FEATURE [Part::Fillet] Fillet053  label="ventcutRight001"
  Base = -> Fusion035
  EdgeLinks = -> Fusion035 [Edge1,Edge3,Edge11,Edge16]
  Edges = 4 edges: [Edge1 r=1,Edge3 r=1,Edge11 r=1,Edge16 r=0.5]
  Placement = pos=(-50,-8.65e-14,75.5) rot=(0,-1,0;4.71239rad)
FEATURE [Part::MultiFuse] Fusion036  label="ventFront"
  Refine = true
  Shapes = -> [Fillet052,Fillet053]
FEATURE [Part::Cut] Cut035  label="topVent"
  Base = -> Fillet051
  Refine = true
  Tool = -> Fusion036
FEATURE [Sketcher::SketchObject] Sketch176
  ArcFitTolerance = 0
  FullyConstrained = true
  MakeInternals = false
  Placement = pos=(0,0,0) rot=(1,0,0;1.5708rad)
  sketch-geometry (40):
    g0: LineSegment StartX=40 StartY=24.5 StartZ=0 EndX=40 EndY=22 EndZ=0
    g1: LineSegment StartX=40 StartY=22 StartZ=0 EndX=42.5 EndY=19.5 EndZ=0
    g2: LineSegment StartX=42.5 StartY=19.5 StartZ=0 EndX=48.7 EndY=19.5 EndZ=0
    g3: LineSegment StartX=48.7 StartY=19.5 StartZ=0 EndX=51.2 EndY=22 EndZ=0
    g4: LineSegment StartX=51.2 StartY=22 StartZ=0 EndX=51.2 EndY=24.5 EndZ=0
    g5: LineSegment StartX=51.2 StartY=24.5 StartZ=0 EndX=40 EndY=24.5 EndZ=0
    g6: LineSegment StartX=52.45 StartY=24.5 StartZ=0 EndX=52.45 EndY=22 EndZ=0
    g7: LineSegment StartX=52.45 StartY=22 StartZ=0 EndX=54.95 EndY=19.5 EndZ=0
    g8: LineSegment StartX=54.95 StartY=19.5 StartZ=0 EndX=61.15 EndY=19.5 EndZ=0
    g9: LineSegment StartX=61.15 StartY=19.5 StartZ=0 EndX=63.65 EndY=22 EndZ=0
    g10: LineSegment StartX=63.65 StartY=22 StartZ=0 EndX=63.65 EndY=24.5 EndZ=0
    g11: LineSegment StartX=63.65 StartY=24.5 StartZ=0 EndX=52.45 EndY=24.5 EndZ=0
    g12: ArcOfCircle CenterX=12.3 CenterY=15.45 CenterZ=0 NormalX=0 NormalY=0 NormalZ=1 AngleXU=0 Radius=1 StartAngle=1.5708 EndAngle=3.14159
    g13: LineSegment StartX=11.3 StartY=15.45 StartZ=0 EndX=11.3 EndY=14.2 EndZ=0
    g14: LineSegment StartX=12.3 StartY=16.45 StartZ=0 EndX=16.8 EndY=16.45 EndZ=0
    g15: ArcOfCircle CenterX=16.8 CenterY=15.45 CenterZ=0 NormalX=0 NormalY=0 NormalZ=1 AngleXU=0 Radius=1 StartAngle=3e-16 EndAngle=1.5708
    g16: ArcOfCircle CenterX=16.8 CenterY=14.2 CenterZ=0 NormalX=0 NormalY=0 NormalZ=1 AngleXU=0 Radius=1 StartAngle=4.71239 EndAngle=6.28319
    g17: ArcOfCircle CenterX=12.3 CenterY=14.2 CenterZ=0 NormalX=0 NormalY=0 NormalZ=1 AngleXU=0 Radius=1 StartAngle=3.14159 EndAngle=4.71239
    g18: LineSegment StartX=12.3 StartY=13.2 StartZ=0 EndX=16.8 EndY=13.2 EndZ=0
    g19: LineSegment StartX=17.8 StartY=15.45 StartZ=0 EndX=17.8 EndY=14.2 EndZ=0
    g20: Circle CenterX=18.9 CenterY=16.475 CenterZ=0 NormalX=0 NormalY=0 NormalZ=1 AngleXU=0 Radius=0.5
    g21: Circle CenterX=21.09 CenterY=16.475 CenterZ=0 NormalX=0 NormalY=0 NormalZ=1 AngleXU=0 Radius=0.5
    g22: Circle CenterX=23.28 CenterY=16.475 CenterZ=0 NormalX=0 NormalY=0 NormalZ=1 AngleXU=0 Radius=0.5
    g23: Circle CenterX=25.47 CenterY=16.475 CenterZ=0 NormalX=0 NormalY=0 NormalZ=1 AngleXU=0 Radius=0.5
    g24: LineSegment StartX=44.8 StartY=16.45 StartZ=0 EndX=49.3 EndY=16.45 EndZ=0
    g25: LineSegment StartX=50.3 StartY=15.45 StartZ=0 EndX=50.3 EndY=14.2 EndZ=0
    g26: LineSegment StartX=49.3 StartY=13.2 StartZ=0 EndX=44.8 EndY=13.2 EndZ=0
    g27: LineSegment StartX=43.8 StartY=15.45 StartZ=0 EndX=43.8 EndY=14.2 EndZ=0
    g28: ArcOfCircle CenterX=44.8 CenterY=15.45 CenterZ=0 NormalX=0 NormalY=0 NormalZ=1 AngleXU=0 Radius=1 StartAngle=1.5708 EndAngle=3.14159
    g29: ArcOfCircle CenterX=49.3 CenterY=15.45 CenterZ=0 NormalX=0 NormalY=0 NormalZ=1 AngleXU=0 Radius=1 StartAngle=3e-16 EndAngle=1.5708
    g30: ArcOfCircle CenterX=49.3 CenterY=14.2 CenterZ=0 NormalX=0 NormalY=0 NormalZ=1 AngleXU=0 Radius=1 StartAngle=4.71239 EndAngle=6.28319
    g31: ArcOfCircle CenterX=44.8 CenterY=14.2 CenterZ=0 NormalX=0 NormalY=0 NormalZ=1 AngleXU=0 Radius=1 StartAngle=3.14159 EndAngle=4.71239
    g32: LineSegment StartX=52.25 StartY=15.58 StartZ=0 EndX=52.25 EndY=14.58 EndZ=0
    g33: LineSegment StartX=53.5 StartY=16.83 StartZ=0 EndX=60.5 EndY=16.83 EndZ=0
    g34: LineSegment StartX=53.5 StartY=13.33 StartZ=0 EndX=60.5 EndY=13.33 EndZ=0
    g35: LineSegment StartX=61.75 StartY=15.58 StartZ=0 EndX=61.75 EndY=14.58 EndZ=0
    g36: ArcOfCircle CenterX=53.5 CenterY=15.58 CenterZ=0 NormalX=0 NormalY=0 NormalZ=1 AngleXU=0 Radius=1.25 StartAngle=1.5708 EndAngle=3.14159
    g37: ArcOfCircle CenterX=60.5 CenterY=15.58 CenterZ=0 NormalX=0 NormalY=0 NormalZ=1 AngleXU=0 Radius=1.25 StartAngle=2e-16 EndAngle=1.5708
    g38: ArcOfCircle CenterX=60.5 CenterY=14.58 CenterZ=0 NormalX=0 NormalY=0 NormalZ=1 AngleXU=0 Radius=1.25 StartAngle=4.7124 EndAngle=6.28319
    g39: ArcOfCircle CenterX=53.5 CenterY=14.58 CenterZ=0 NormalX=0 NormalY=0 NormalZ=1 AngleXU=0 Radius=1.25 StartAngle=3.14159 EndAngle=4.71239
  constraints (132):
    c: Coincident(g0,g1)
    c: Coincident(g1,g2)
    c: Horizontal(g2)
    c: Coincident(g2,g3)
    c: Coincident(g3,g4)
    c: Vertical(g4)
    c: Coincident(g4,g5)
    c: Coincident(g5,g0)
    c: Coincident(g6,g7)
    c: Coincident(g7,g8)
    c: Horizontal(g8)
    c: Coincident(g8,g9)
    c: Coincident(g9,g10)
    c: Vertical(g10)
    c: Coincident(g10,g11)
    c: Coincident(g11,g6)
    c: Horizontal(g11)
    c: Horizontal(g5)
    c: Vertical(g0)
    c: Vertical(g6)
    c: DistanceX(g0) = 40
    c: DistanceX(g0,g4) = 11.2
    c: DistanceY(g6,g4) = 0
    c: DistanceY(g0,g0) = 2.5
    c: DistanceY(g3,g0) = 0
    c: DistanceY(g6,g3) = 0
    c: DistanceY(g9,g6) = 0
    c: DistanceY(g1,g0) = 2.5
    c: DistanceX(g0,g1) = 2.5
    c: DistanceX(g2,g3) = 2.5
    c: DistanceX(g4,g6) = 1.25
    c: DistanceY(g7,g2) = 0
    c: DistanceX(g6,g7) = 2.5
    c: DistanceX(g8,g9) = 2.5
    c: DistanceX(g6,g10) = 11.2
    c: DistanceY(g0) = 24.5
    c: Coincident(g13,g12)
    c: Vertical(g13)
    c: Horizontal(g14)
    c: Coincident(g15,g14)
    c: Coincident(g17,g13)
    c: Coincident(g18,g17)
    c: Coincident(g18,g16)
    c: Horizontal(g18)
    c: Coincident(g19,g15)
    c: Coincident(g19,g16)
    c: Vertical(g19)
    c: Coincident(g12,g14)
    c: Radius(g12) = 1
    c: Angle(g12) = 1.5708
    c: Angle(g15) = 1.5708
    c: Angle(g16) = 1.5708
    c: Angle(g17) = 1.5708
    c: DistanceX(g17) = 12.3
    c: DistanceY(g17) = 13.2
    c: DistanceX(g13) = 11.3
    c: DistanceY(g17,g13) = 0
    c: DistanceY(g12,g12) = 0
    c: DistanceX(g15,g14) = 0
    c: Radius(g15) = 1
    c: Radius(g16) = 1
    c: DistanceX(g16,g16) = 0
    c: DistanceX(g12,g14) = 4.5
    c: DistanceX(g20) = 18.9
    c: Radius(g20) = 0.5
    c: DistanceY(g20) = 16.475
    c: DistanceX(g20,g21) = 2.19
    c: DistanceY(g20,g21) = 0
    c: DistanceY(g22,g21) = 0
    c: DistanceY(g23,g22) = 0
    c: DistanceX(g21,g22) = 2.19
    c: Radius(g21) = 0.5
    c: Radius(g22) = 0.5
    c: Radius(g23) = 0.5
    c: DistanceX(g22,g23) = 2.19
    c: DistanceY(g17,g12) = 1.25
    c: Horizontal(g24)
    c: Vertical(g25)
    c: Vertical(g27)
    c: Coincident(g27,g28)
    c: Coincident(g27,g31)
    c: Coincident(g26,g31)
    c: Coincident(g26,g30)
    c: Coincident(g25,g30)
    c: Coincident(g25,g29)
    c: Coincident(g24,g29)
    c: Coincident(g24,g28)
    c: Angle(g28) = 1.5708
    c: Angle(g29) = 1.5708
    c: Angle(g31) = 1.5708
    c: Angle(g30) = 1.5708
    c: DistanceY(g12,g28) = 0
    c: DistanceY(g28,g27) = 0
    c: Radius(g28) = 1
    c: DistanceY(g27,g31) = 0
    c: Radius(g31) = 1
    c: Radius(g30) = 1
    c: Radius(g29) = 1
    c: DistanceY(g27,g17) = 0
    c: DistanceY(g25,g30) = 0
    c: Horizontal(g26)
    c: DistanceX(g29,g24) = 0
    c: DistanceX(g26,g26) = 4.5
    c: Vertical(g32)
    c: Horizontal(g33)
    c: Horizontal(g34)
    c: Vertical(g35)
    c: Coincident(g36,g32)
    c: Coincident(g36,g33)
    c: Coincident(g37,g33)
    c: Coincident(g39,g32)
    c: Coincident(g39,g34)
    c: Coincident(g34,g38)
    c: Coincident(g35,g38)
    c: Coincident(g35,g37)
    c: DistanceX(g36) = 53.5
    c: DistanceY(g36) = 15.58
    c: DistanceX(g36,g39) = 0
    c: DistanceY(g39,g36) = 1
    c: Radius(g36) = 1.25
    c: Radius(g38) = 1.25
    c: Radius(g37) = 1.25
    c: DistanceX(g39,g34) = 0
    c: DistanceX(g36,g33) = 0
    c: DistanceY(g36,g37) = 0
    c: DistanceY(g38,g39) = 0
    c: DistanceY(g39,g32) = 0
    c: DistanceX(g36,g37) = 7
    c: DistanceX(g12,g28) = 32.5
    c: DistanceY(g35,g38) = 0
    c: DistanceY(g37,g35) = 0
    c: Angle(g36) = 1.5708
FEATURE [Part::Extrusion] Extrude178  label="lightBottomCutDone005"
  Base = -> Sketch176
  Dir = (0,-1,2e-16)
  DirMode = 2
  FaceMakerClass = Part::FaceMakerBullseye
  FaceMakerMode = 3
  LengthFwd = 10
  LengthRev = 0
  Placement = pos=(8.25,84,74) rot=(-1,0,0;3.14159rad)
  Solid = true
  Symmetric = false
FEATURE [Part::MultiFuse] Fusion037  label="topPihold"
  Refine = true
  Shapes = -> [Cut035,Fillet044]
FEATURE [Part::Cut] Cut036  label="topPropercut"
  Base = -> Fusion037
  Refine = true
  Tool = -> Extrude178
FEATURE [Part::MultiFuse] Fusion038  label="batteryHoldm2"
  Refine = true
  Shapes = -> [Extrude163,Extrude177]
FEATURE [Part::MultiFuse] Fusion039  label="topCoverBatteryHold"
  Refine = true
  Shapes = -> [Cut036,Fusion038]
FEATURE [Part::Feature] Part__Feature067  label="logoTopCut001"
  Placement = pos=(14,32.5,85) rot=(-1,0,0;1.5708rad)
  shape: bbox 22.79 x 17.08 x 8 mm, 886 faces (baked)
FEATURE [Part::Cut] Cut037  label="toplogocut001"
  Base = -> Fusion039
  Refine = true
  Tool = -> Part__Feature067
FEATURE [Part::Feature] Part__Feature3697  label="logoTopCut002"
  Placement = pos=(14,32.5,85) rot=(-1,0,0;1.5708rad)
  shape: bbox 22.79 x 17.08 x 8 mm, 886 faces (baked)
FEATURE [Part::Scale] Scale002
  Base = -> Part__Feature3697
  Placement = pos=(5,23,66) rot=(1,0,0;4.71239rad)
  Uniform = true
  UniformScale = 1.2
  XScale = 1
  YScale = 1
  ZScale = 1
FEATURE [Part::Cut] Cut038  label="topCoverlogobackcut"
  Base = -> Cut037
  Refine = true
  Tool = -> Scale002
FEATURE [Part::Fillet] Fillet054  label="topCoverfillet"
  Base = -> Cut038
  EdgeLinks = -> Cut038 [Edge79,Edge80,Edge81,Edge82,Edge174,Edge175,Edge176,Edge177]
  Edges = 8 edges r=1: [Edge79,Edge80,Edge81,Edge82,Edge174,Edge175,Edge176,Edge177]
FEATURE [Part::Cylinder] Cylinder020
  Angle = 360
  AttacherType = Attacher::AttachEngine3D
  FirstAngle = 0
  Height = 7
  Placement = pos=(29,29,-5) rot=(0,0,1;0rad)
  Radius = 2.5
  SecondAngle = 0
FEATURE [Part::Cylinder] Cylinder021
  Angle = 360
  AttacherType = Attacher::AttachEngine3D
  FirstAngle = 0
  Height = 7
  Placement = pos=(29,61,-5) rot=(0,0,1;0rad)
  Radius = 2.5
  SecondAngle = 0
FEATURE [Part::Cylinder] Cylinder022
  Angle = 360
  AttacherType = Attacher::AttachEngine3D
  FirstAngle = 0
  Height = 7
  Placement = pos=(61,61,-5) rot=(0,0,1;0rad)
  Radius = 2.5
  SecondAngle = 0
FEATURE [Part::Cylinder] Cylinder023
  Angle = 360
  AttacherType = Attacher::AttachEngine3D
  FirstAngle = 0
  Height = 7
  Placement = pos=(61,29,-5) rot=(0,0,1;0rad)
  Radius = 2.5
  SecondAngle = 0
FEATURE [Part::MultiFuse] Fusion040
  Refine = true
  Shapes = -> [Cylinder020,Cylinder021,Cylinder022,Cylinder023]
FEATURE [Part::Cut] Cut039  label="baseFanmounthole"
  Base = -> Fusion028
  Refine = true
  Tool = -> Fusion040
FEATURE [Part::Box] Box033  label="Cube009"
  AttacherType = Attacher::AttachEngine3D
  Height = 19
  Length = 8
  Placement = pos=(28,21,11) rot=(0,1,0;4.71239rad)
  Width = 5
FEATURE [Part::Box] Box034  label="Cube010"
  AttacherType = Attacher::AttachEngine3D
  Height = 13
  Length = 8
  Placement = pos=(17,16,19) rot=(0,-1,0;3.14159rad)
  Width = 5
FEATURE [Part::Box] Box035  label="Cube011"
  AttacherType = Attacher::AttachEngine3D
  Height = 22
  Length = 8
  Placement = pos=(81,21,48) rot=(0,1,0;4.71239rad)
  Width = 5
FEATURE [Part::Box] Box036  label="Cube012"
  AttacherType = Attacher::AttachEngine3D
  Height = 52
  Length = 8
  Placement = pos=(81,14,56) rot=(0,-1,0;3.14159rad)
  Width = 7
FEATURE [Part::MultiFuse] Fusion041  label="ipsHolders"
  Refine = true
  Shapes = -> [Box033,Box034,Box035,Box036]
FEATURE [Part::Cylinder] Cylinder024
  Angle = 360
  AttacherType = Attacher::AttachEngine3D
  FirstAngle = 0
  Height = 10
  Placement = pos=(23.1,19,14.7) rot=(1,0,0;4.71239rad)
  Radius = 1.1
  SecondAngle = 0
FEATURE [Part::Cylinder] Cylinder025
  Angle = 360
  AttacherType = Attacher::AttachEngine3D
  FirstAngle = 0
  Height = 10
  Placement = pos=(63.9,19,51.5) rot=(1,0,0;4.71239rad)
  Radius = 1.1
  SecondAngle = 0
FEATURE [Part::MultiFuse] Fusion042  label="m2cyl"
  Refine = true
  Shapes = -> [Cylinder024,Cylinder025]
FEATURE [Part::Cut] Cut040  label="ipsm2cut"
  Base = -> Fusion041
  Refine = true
  Tool = -> Fusion042
FEATURE [Part::Box] Box037  label="Cube013"
  AttacherType = Attacher::AttachEngine3D
  Height = 8
  Length = 8
  Placement = pos=(73,14,36) rot=(0,0,1;0rad)
  Width = 47
FEATURE [Part::Cylinder] Cylinder026
  Angle = 360
  AttacherType = Attacher::AttachEngine3D
  FirstAngle = 0
  Height = 10
  Placement = pos=(72,37.25,40.4) rot=(0,1,0;1.5708rad)
  Radius = 1.1
  SecondAngle = 0
FEATURE [Part::Cylinder] Cylinder027
  Angle = 360
  AttacherType = Attacher::AttachEngine3D
  FirstAngle = 0
  Height = 10
  Placement = pos=(72,57.57,40.35) rot=(0,1,0;1.5708rad)
  Radius = 1.1
  SecondAngle = 0
FEATURE [Part::MultiFuse] Fusion043  label="bmem2"
  Refine = true
  Shapes = -> [Cylinder026,Cylinder027]
FEATURE [Part::Cut] Cut041  label="bmem2cut"
  Base = -> Box037
  Refine = true
  Tool = -> Fusion043
FEATURE [Part::MultiFuse] Fusion044  label="ipsbmeHold"
  Refine = true
  Shapes = -> [Cut040,Cut041]
FEATURE [Part::MultiFuse] Fusion045  label="bottomSensorHold"
  Refine = true
  Shapes = -> [Fillet002,Fusion044]
FEATURE [Part::Fillet] Fillet055
  Base = -> Fusion045
  EdgeLinks = -> Fusion045 [Edge45,Edge46,Edge47,Edge49,Edge50,Edge51,Edge52,Edge491,Edge492,Edge495,Edge496,Edge497,Edge498,Edge499,Edge501,Edge502,Edge503,Edge504,Edge505,Edge506,Edge507,Edge508,Edge510,Edge511,Edge514,Edge516,Edge517,Edge518,Edge519,Edge520,Edge1395,Edge1396,Edge1397,Edge1398,Edge1399,Edge1400,Edge1402,Edge1404,Edge1405,Edge1406,+7 more]
  Edges = 47 edges: [Edge45 r=1,Edge46 r=1,Edge47 r=1,Edge49 r=1,Edge50 r=1,Edge51 r=1,Edge52 r=1,Edge491 r=3,Edge492 r=1,Edge495 r=1,Edge496 r=1,Edge497 r=1.5,Edge498 r=1,Edge499 r=1,Edge501 r=1,Edge502 r=1,Edge503 r=1,Edge504 r=3,Edge505 r=1,Edge506 r=1,Edge507 r=1,Edge508 r=1,Edge510 r=3,Edge511 r=1,Edge514 r=1,Edge516 r=1,Edge517 r=1,Edge518 r=1,Edge519 r=1,Edge520 r=1,Edge1395 r=1,Edge1396 r=1,Edge1397 r=1,Edge1398 r=1,Edge1399 r=1,Edge1400 r=1,Edge1402 r=1,Edge1404 r=2.5,Edge1405 r=2.5,Edge1406 r=2,Edge1408 r=1,Edge1410 r=1,Edge1412 r=1,Edge1413 r=2.5,Edge1416 r=1,Edge1417 r=1,Edge1419 r=2.5]
FEATURE [Part::Cylinder] Cylinder028
  Angle = 360
  AttacherType = Attacher::AttachEngine3D
  FirstAngle = 0
  Height = 20
  Placement = pos=(20,12,-8) rot=(0,0,1;0rad)
  Radius = 1.65
  SecondAngle = 0
FEATURE [Part::Cylinder] Cylinder029
  Angle = 360
  AttacherType = Attacher::AttachEngine3D
  FirstAngle = 0
  Height = 20
  Placement = pos=(70,12,-8) rot=(0,0,1;0rad)
  Radius = 1.65
  SecondAngle = 0
FEATURE [Part::Cylinder] Cylinder030
  Angle = 360
  AttacherType = Attacher::AttachEngine3D
  FirstAngle = 0
  Height = 20
  Placement = pos=(70,78,-8) rot=(0,0,1;0rad)
  Radius = 1.65
  SecondAngle = 0
FEATURE [Part::Cylinder] Cylinder031
  Angle = 360
  AttacherType = Attacher::AttachEngine3D
  FirstAngle = 0
  Height = 20
  Placement = pos=(20,78,-8) rot=(0,0,1;0rad)
  Radius = 1.65
  SecondAngle = 0
FEATURE [Part::MultiFuse] Fusion046
  Refine = true
  Shapes = -> [Cylinder028,Cylinder029,Cylinder030,Cylinder031]
FEATURE [Part::Cylinder] Cylinder032
  Angle = 360
  AttacherType = Attacher::AttachEngine3D
  FirstAngle = 0
  Height = 20
  Placement = pos=(20,12,-8) rot=(0,0,1;0rad)
  Radius = 1.65
  SecondAngle = 0
FEATURE [Part::Cylinder] Cylinder033
  Angle = 360
  AttacherType = Attacher::AttachEngine3D
  FirstAngle = 0
  Height = 20
  Placement = pos=(70,12,-8) rot=(0,0,1;0rad)
  Radius = 1.65
  SecondAngle = 0
FEATURE [Part::Cylinder] Cylinder034
  Angle = 360
  AttacherType = Attacher::AttachEngine3D
  FirstAngle = 0
  Height = 20
  Placement = pos=(70,78,-8) rot=(0,0,1;0rad)
  Radius = 1.65
  SecondAngle = 0
FEATURE [Part::Cylinder] Cylinder035
  Angle = 360
  AttacherType = Attacher::AttachEngine3D
  FirstAngle = 0
  Height = 20
  Placement = pos=(20,78,-8) rot=(0,0,1;0rad)
  Radius = 1.65
  SecondAngle = 0
FEATURE [Part::MultiFuse] Fusion047
  Refine = true
  Shapes = -> [Cylinder032,Cylinder033,Cylinder034,Cylinder035]
FEATURE [Part::Cylinder] Cylinder036
  Angle = 360
  AttacherType = Attacher::AttachEngine3D
  FirstAngle = 0
  Height = 20
  Placement = pos=(20,12,-8) rot=(0,0,1;0rad)
  Radius = 1.65
  SecondAngle = 0
FEATURE [Part::Cylinder] Cylinder037
  Angle = 360
  AttacherType = Attacher::AttachEngine3D
  FirstAngle = 0
  Height = 20
  Placement = pos=(70,12,-8) rot=(0,0,1;0rad)
  Radius = 1.65
  SecondAngle = 0
FEATURE [Part::Cylinder] Cylinder038
  Angle = 360
  AttacherType = Attacher::AttachEngine3D
  FirstAngle = 0
  Height = 20
  Placement = pos=(70,78,-8) rot=(0,0,1;0rad)
  Radius = 1.65
  SecondAngle = 0
FEATURE [Part::Cylinder] Cylinder039
  Angle = 360
  AttacherType = Attacher::AttachEngine3D
  FirstAngle = 0
  Height = 20
  Placement = pos=(20,78,-8) rot=(0,0,1;0rad)
  Radius = 1.65
  SecondAngle = 0
FEATURE [Part::MultiFuse] Fusion048
  Refine = true
  Shapes = -> [Cylinder036,Cylinder037,Cylinder038,Cylinder039]
FEATURE [Part::Cut] Cut042
  Base = -> Fillet055
  Refine = true
  Tool = -> Fusion048
FEATURE [Part::Cut] Cut043
  Base = -> Cut039
  Refine = true
  Tool = -> Fusion047
FEATURE [Part::Cylinder] Cylinder040
  Angle = 360
  AttacherType = Attacher::AttachEngine3D
  FirstAngle = 0
  Height = 20
  Placement = pos=(20,12,-8) rot=(0,0,1;0rad)
  Radius = 1.65
  SecondAngle = 0
FEATURE [Part::Cylinder] Cylinder041
  Angle = 360
  AttacherType = Attacher::AttachEngine3D
  FirstAngle = 0
  Height = 20
  Placement = pos=(70,12,-8) rot=(0,0,1;0rad)
  Radius = 1.65
  SecondAngle = 0
FEATURE [Part::Cylinder] Cylinder042
  Angle = 360
  AttacherType = Attacher::AttachEngine3D
  FirstAngle = 0
  Height = 20
  Placement = pos=(70,78,-8) rot=(0,0,1;0rad)
  Radius = 1.65
  SecondAngle = 0
FEATURE [Part::Cylinder] Cylinder043
  Angle = 360
  AttacherType = Attacher::AttachEngine3D
  FirstAngle = 0
  Height = 20
  Placement = pos=(20,78,-8) rot=(0,0,1;0rad)
  Radius = 1.65
  SecondAngle = 0
FEATURE [Part::MultiFuse] Fusion049
  Refine = true
  Shapes = -> [Cylinder040,Cylinder041,Cylinder042,Cylinder043]
FEATURE [Part::Cut] Cut044
  Base = -> Scale
  Refine = true
  Tool = -> Fusion049
FEATURE [App::Part] Part001  label="Base"
  Group = -> [Cylinder003,Part__Feature3679,Fusion024,Cylinder004,Part__Feature3694,Fusion026,Cylinder005,Part__Feature3695,Fusion027,Sketch002,Extrude001,Fusion045,Box033,Fusion042,Cut041,Cylinder036,Cylinder037,Cylinder038,Cylinder039,Fusion048,Cylinder026,Cylinder024,Box037,Box036,Box035,Fusion041,Fusion044,Fusion043,Fillet055,Cut040,Clone,Sketch,Extrude,Fillet001,Fusion,Fillet002,Cylinder027,Cylinder025,+28 more]
  Origin = -> Origin095
